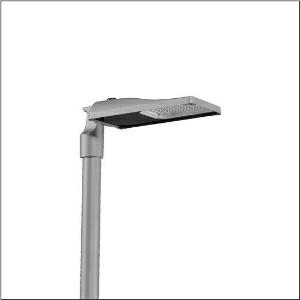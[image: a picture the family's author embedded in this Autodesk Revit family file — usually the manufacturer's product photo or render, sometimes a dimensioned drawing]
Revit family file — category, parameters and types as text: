
# Revit family: streetlight_sl_31_mini___st1_0a_5xh2d3as08ha_8082
name_source: partatom
category: Lighting Fixtures
units: mm (PartAtom-declared; Revit-internal decimal feet)

## family parameters
Cut with Voids When Loaded = No
Host = Face
Light Source = No
Part Type = Normal
Room Calculation Point = No
Round Connector Dimension = Use Diameter
Shared = No

## types (1)
- --- (1 x LED, 9230 lm, 68.3 W, 3000K)
    Apparent Load = 68 VA
    CIE Flux Codes = 37 72 97 100 100
    Color Rendering = 70
    Color Temperature = 3000K
    Default Elevation = 1800 mm
    Description = Streetlight SL 31 mini D4i mast luminaire for post-top, side-entry; light control with lens of PMMA; light distribution: ST1.0a, direct asymmetric distribution, for standard-compliant lighting for roads and squares; LED: luminous flux: 9.230lm, light colour: 730, colour temperature: 3000K; luminous efficacy: 135,1lm/W; control: pre-setting: logarithmic dimming characteristic, flexible luminous flux parameterisation, time-dependent luminous flux control, constant luminous flux control, power reduction, intelligent temperature release in ECG and LED module, overheat protection; luminaire housing, of diecast aluminium, SITECO metallic grey (DB 702S), corrosivity category C5 high according to DIN EN ISO 12944; cover of toughened safety glass, transparent, mast flange of diecast aluminium, SITECO metallic grey (DB 702S), spigot size: 76/60mm, mast flange included unmounted; cable length: 8,5m, connection cable pre-assembled; mains connection: 220..240V, AC, 50/60Hz; power consumption (at start of service life): 68,3W / (at end of service life): 74,5W / (with reduced operation 50%): 29,5W; protection rating (complete): IP66; insulation class (complete): insulation class II (safety insulation); impact resistance: IK10; certification: CE, ENEC, ENEC+, VDE, UKCA, ZD4i; permissible operating ambient temperature for outdoor applications: -40..+50°C; packaging unit: 1 piece

Light Distribution: ST1.0a
    Height = 76 mm
    Lamp = 1 x LED
    Lamp Light Flux = 9230 lm
    Lamp Power = 68.3 W
    Lamp count = 1
    Length = 547 mm
    Luminous efficacy = 135 lm/W
    Manufacturer = Siteco
    ModVariant = No
    Model = 5XH2D3AS08HA
    Number of Poles = 1
    OnlyDefault = Yes
    Power Factor = 1
    Product Name = Streetlight SL 31 mini | ST1.0a
    Product group = mast luminaire | pylon top
    ProductGroupID = 6100
    Protection Class = Protection class II
    Protection Degree = IP 66
    RLX_Detail_Level = 1
    RLX_Emergency_Light_Flux = 0 lm
    RLX_Emergency_Type = 0
    RLX_Emergency_Type_DB = No
    RlxData = <blob elided: 39353 chars, md5=bf4a36f2>
    Socket = socket
    Standby Power = 0 W
    System Light Flux = 9230 lm
    System Power = 68 W
    Type Comments = factory setting: luminous flux: 100 % | dim-lin: 254 | 692 mA
    Type Image = l_1300330.jpg
    URL = http://relux.com
    VarID = @adj_020625
    Voltage = 0 V
    Weight = 0.00 kg
    Width = 265 mm

## geometry (parser evidence)
native form markers: Blend x4, Sweep x11
no freeform markers — native parametric forms only
